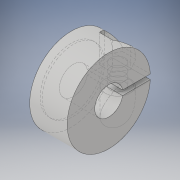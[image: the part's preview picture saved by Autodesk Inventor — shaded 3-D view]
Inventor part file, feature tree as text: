
AUTODESK INVENTOR PART (.ipt)
format: ipt  version: 2019 (Build 230136000, 136)  size: 164,864 bytes
history: native  units: mm
features: sketch x4, extrude x3, plane x2, hole x1
ambient origin geometry x8: Origin, YZ Plane, XZ Plane, XY Plane, X Axis, Y Axis, Z Axis, Center Point
bodies: Solid1 (feature_tree)
feature tree (10):
  extrude  "Extrusion1"  Depth=20.0mm
  extrude  "Extrusion3"  Depth=3.490659mm
  plane  "Work Plane1"
  extrude  "Extrusion4"  Depth=15.0mm
  plane  "Work Plane2"
  hole  "Hole1"  [1 undecoded]
  sketch  "Sketch1"  dims[d0=6.75mm d1=20.0mm]
  sketch  "Sketch3"  dims[d2=13.962634mm d3=3.490659mm]
  sketch  "Sketch4"  dims[d4=9.0mm d5=0.0mm d9=15.0mm]
  sketch  "Sketch5"  dims[d10=0.5mm d11=0.0mm d12=10.0mm d13=5.5mm d14=7.5mm d15=0.0mm d16=-20.0mm d17=3.5mm d18=6.0mm d19=6.0mm d20=7.5mm d21=90.0deg d22=8.0mm d23=0.0mm]
note: 1 required parameter value undecoded (feature->parameter linkage not recoverable at this tier; creation-order binding heuristic only, values carry confidence <= 0.55)
